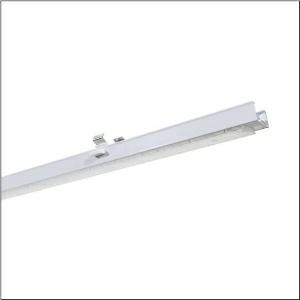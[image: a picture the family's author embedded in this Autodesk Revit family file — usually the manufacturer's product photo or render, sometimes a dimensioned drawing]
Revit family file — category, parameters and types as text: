
# Revit family: sanierungs-leuchteneinsatz_31_gen_2_51re12mb58b_56d9
name_source: partatom
category: Lighting Fixtures
units: mm (PartAtom-declared; Revit-internal decimal feet)

## family parameters
Cut with Voids When Loaded = No
Host = Face
Light Source = No
Part Type = Normal
Room Calculation Point = No
Round Connector Dimension = Use Diameter
Shared = No

## types (1)
- --- (1 x LED, 8000 lm, 50 W, 5000K)
    Apparent Load = 50 VA
    CIE Flux Codes = 65 91 98 99 100
    Color Rendering = 80
    Color Temperature = 5000K
    Default Elevation = 1800 mm
    Description = Refurbishment luminaire insert Gen.2, luminaire insert, of extruded aluminium section, coated, traffic white (RAL 9016), length: 1.472mm, width: 91mm, height: 53mm, LED rated luminous flux: 8.000lm, light colour: 850, control gear: ON/OFF Multilumen, with system connector: socket, mains connection: 220..240V, AC, 50/60Hz, luminous flux adjustable on luminaire in four steps (4130/5610/6850/8000lm), connected load according to luminous flux setting (25/34/42/50W), primary light control with lens, of plastic, primary optical cover: cover, of PMMA, light emission: direct distribution, protection rating (complete): IP20, insulation class (complete): insulation class I (protective earthing), certification: CE, UKCA, impact resistance: IK02, permissible ambient temperature for indoor applications: -20..+40°C, packaging unit: 1 piece
    Height = 58 mm
    Lamp = 1 x LED
    Lamp Light Flux = 8000 lm
    Lamp Power = 50 W
    Lamp count = 1
    Length = 1472 mm
    Luminous efficacy = 160 lm/W
    Manufacturer = Siteco
    ModVariant = No
    Model = 51RE12MB58B
    Mounting Place = Ceiling
    Mounting Type = Pendant
    Number of Poles = 1
    OnlyDefault = Yes
    Power Factor = 1
    Product Name = Sanierungs-Leuchteneinsatz 31 Gen.2
    Product group = luminaire insert
    ProductGroupID = 902
    Protection Class = Protection class I
    Protection Degree = IP 20
    RLX_Detail_Level = 1
    RlxData = <blob elided: 20329 chars, md5=d524d18e>
    Socket = socket
    Standby Power = 0 W
    System Light Flux = 8000 lm
    System Power = 50 W
    Type Comments = factory setting: luminous flux: 100 % | (ON | ON) | 300 mA
    Type Image = l_1266702.jpg
    URL = http://relux.com
    VarID = @adj_053725
    Voltage = 0 V
    Weight = 0.00 kg
    Width = 65 mm

## geometry (parser evidence)
native form markers: Blend x4, Sweep x11
no freeform markers — native parametric forms only
